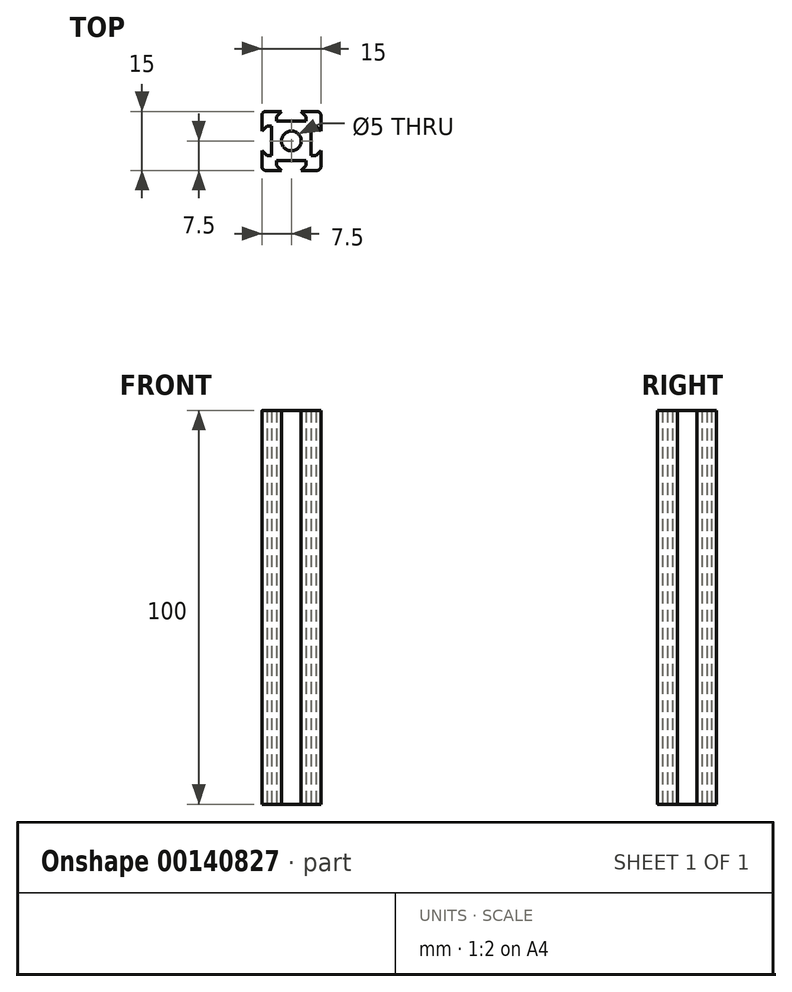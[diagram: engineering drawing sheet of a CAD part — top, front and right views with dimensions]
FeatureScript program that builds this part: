
annotation { "Feature Type Name" : "Feature", "Feature Type Description" : "" }
export const myFeature = defineFeature(function(context is Context, id is Id, definition is map)
    precondition{}
    {
        {
            var Q0;
            Q0=qCreatedBy(makeId("Top.planeOp"),FACE);
            var sketch = newSketch(context, id + "F0", { "sketchPlane" : qUnion([Q0])});
            skLineSegment(sketch, "E0.top", {"start": v(6.5, 7.5) * mm, "end": v(2.5, 7.5) * mm});
            skPoint(sketch, "E0.middle", {"position": v(0, 0) * mm});
            skLineSegment(sketch, "E1", {"start": v(6.25, 3.75) * mm, "end": v(7.5, 2.5) * mm});
            skLineSegment(sketch, "E2", {"start": v(3.75, 6.25) * mm, "end": v(2.5, 7.5) * mm});
            skLineSegment(sketch, "E3.trimOffspring", {"start": v(7.5, 2.5) * mm, "end": v(7.5, 6.5) * mm});
            skArc(sketch, "E4", {"start": v(2.5, 0) * mm, "mid": v(1.77, 1.77) * mm, "end": v(0, 2.5) * mm});
            skLineSegment(sketch, "E5", {"start": v(3.75, 6.25) * mm, "end": v(3.75, 5) * mm});
            skLineSegment(sketch, "E6", {"start": v(6.25, 3.75) * mm, "end": v(5, 3.75) * mm});
            skLineSegment(sketch, "E7", {"start": v(0, 5) * mm, "end": v(0, 0) * mm});
            skLineSegment(sketch, "E8", {"start": v(0, 0) * mm, "end": v(5, 0) * mm});
            skLineSegment(sketch, "E9", {"start": v(5, 3.75) * mm, "end": v(5, 0) * mm});
            skLineSegment(sketch, "E10", {"start": v(3.75, 5) * mm, "end": v(0, 5) * mm});
            skPoint(sketch, "E11.visualSharp", {"position": v(7.5, 7.5) * mm});
            skArc(sketch, "E11.filletArc", {"start": v(7.5, 6.5) * mm, "mid": v(7.2, 7.2) * mm, "end": v(6.5, 7.5) * mm});
            skSolve(sketch);
        }
        {
            assignVariable(context, id + "F1", {"name" : "length", "anyValue" : 100});
        }
        {
            var Q0;
            Q0=makeQuery(id+"F0.imprint","IMPRINT",FACE,{"disambiguationData":[TD([[makeQuery(id+"F0.imprint","IMPRINT",EDGE,{"derivedFrom":sQuery(id+"F0.wireOp",EDGE,"E0.top")}),1.0]])]});
            extrude(context, id + "F2", {"entities" : qUnion([Q0]), "endBound" : BoundingType.SYMMETRIC, "depth" : (getVariable(context, 'length')) * mm});
        }
        {
            var Q0;
            Q0=makeQuery(id+"F2.opExtrude","SWEPT_BODY",BODY,{"disambiguationData":[OSD([sQuery(id+"F0.wireOp",EDGE,"E0.top"),sQuery(id+"F0.wireOp",EDGE,"E1"),sQuery(id+"F0.wireOp",EDGE,"E2"),sQuery(id+"F0.wireOp",EDGE,"E3.trimOffspring"),sQuery(id+"F0.wireOp",EDGE,"E4"),sQuery(id+"F0.wireOp",EDGE,"E5"),sQuery(id+"F0.wireOp",EDGE,"E6"),sQuery(id+"F0.wireOp",EDGE,"E7"),sQuery(id+"F0.wireOp",EDGE,"E8"),sQuery(id+"F0.wireOp",EDGE,"E9"),sQuery(id+"F0.wireOp",EDGE,"E10"),sQuery(id+"F0.wireOp",EDGE,"E11.filletArc")])]});
            var Q1;
            Q1=qCreatedBy(makeId("Right.planeOp"),FACE);
            mirror(context, id + "F3", {"operationType" : NewBodyOperationType.ADD, "entities" : qUnion([Q0]), "mirrorPlane" : qUnion([Q1])});
        }
        {
            var Q0;
            Q0=makeQuery(id+"F2.opExtrude","SWEPT_BODY",BODY,{"disambiguationData":[OSD([sQuery(id+"F0.wireOp",EDGE,"E0.top"),sQuery(id+"F0.wireOp",EDGE,"E1"),sQuery(id+"F0.wireOp",EDGE,"E2"),sQuery(id+"F0.wireOp",EDGE,"E3.trimOffspring"),sQuery(id+"F0.wireOp",EDGE,"E4"),sQuery(id+"F0.wireOp",EDGE,"E5"),sQuery(id+"F0.wireOp",EDGE,"E6"),sQuery(id+"F0.wireOp",EDGE,"E7"),sQuery(id+"F0.wireOp",EDGE,"E8"),sQuery(id+"F0.wireOp",EDGE,"E9"),sQuery(id+"F0.wireOp",EDGE,"E10"),sQuery(id+"F0.wireOp",EDGE,"E11.filletArc")])]});
            var Q1;
            Q1=qCreatedBy(makeId("Front.planeOp"),FACE);
            mirror(context, id + "F4", {"operationType" : NewBodyOperationType.ADD, "entities" : qUnion([Q0]), "mirrorPlane" : qUnion([Q1])});
        }
    });
